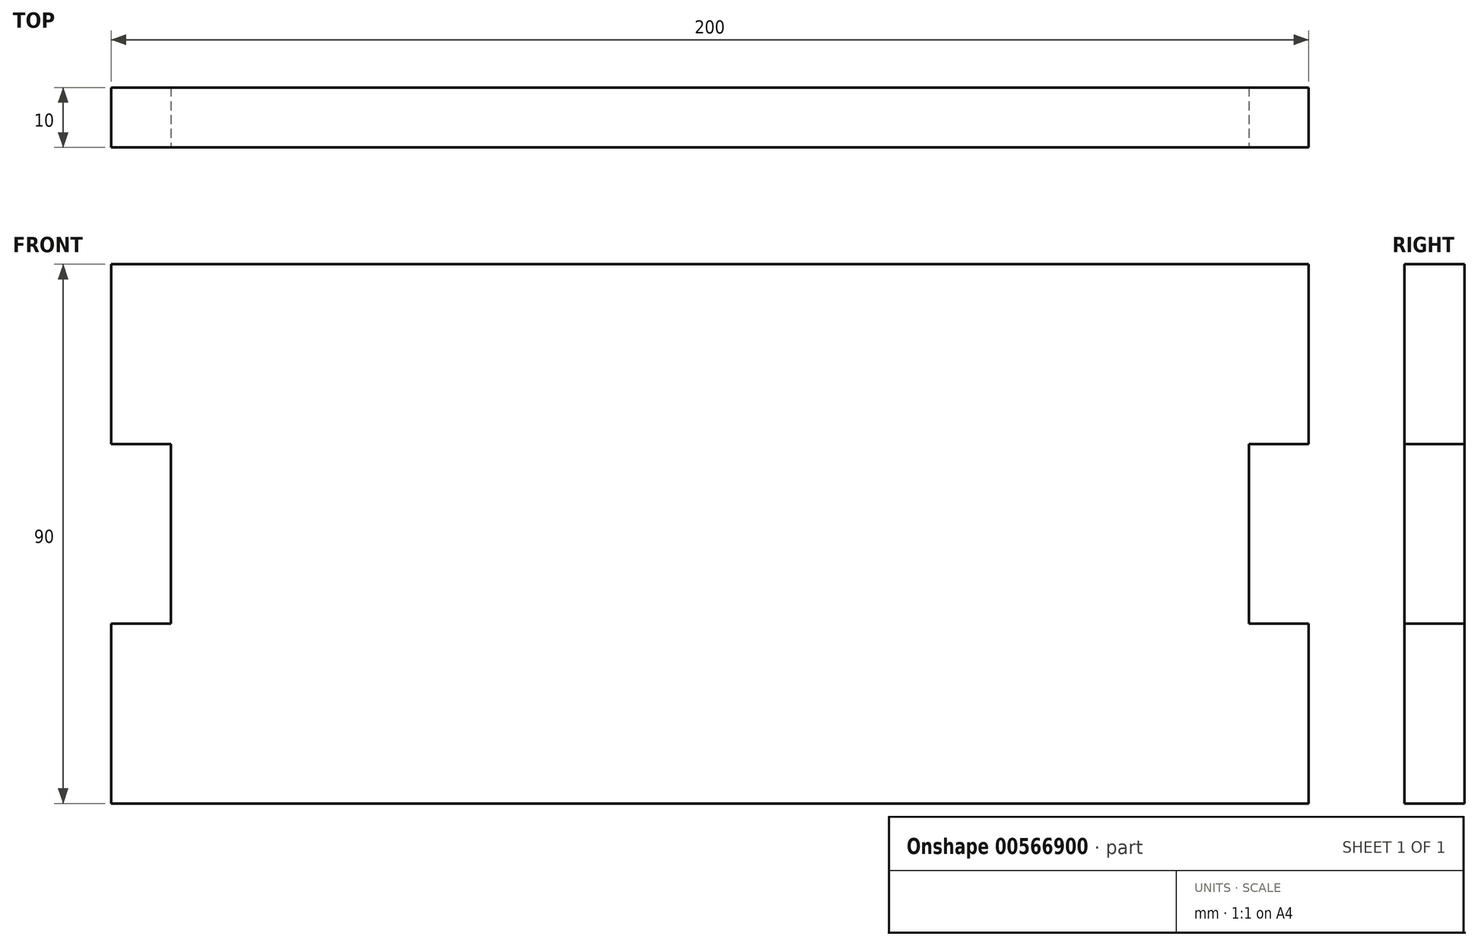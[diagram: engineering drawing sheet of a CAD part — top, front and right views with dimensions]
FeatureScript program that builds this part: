
annotation { "Feature Type Name" : "Feature", "Feature Type Description" : "" }
export const myFeature = defineFeature(function(context is Context, id is Id, definition is map)
    precondition{}
    {
        {
            var Q0;
            Q0=qCreatedBy(makeId("Front.planeOp"),FACE);
            var sketch = newSketch(context, id + "F0", { "sketchPlane" : qUnion([Q0])});
            skLineSegment(sketch, "E0", {"start": v(0, 0) * mm, "end": v(100, 0) * mm});
            skLineSegment(sketch, "E1", {"start": v(100, 0) * mm, "end": v(100, 90) * mm, "construction": true});
            skLineSegment(sketch, "E2", {"start": v(100, 90) * mm, "end": v(0, 90) * mm});
            skLineSegment(sketch, "E3", {"start": v(0, 90) * mm, "end": v(0, 60) * mm});
            skLineSegment(sketch, "E4", {"start": v(0, 0) * mm, "end": v(0, 30) * mm});
            skLineSegment(sketch, "E5", {"start": v(0, 30) * mm, "end": v(10, 30) * mm});
            skLineSegment(sketch, "E6", {"start": v(10, 30) * mm, "end": v(10, 60) * mm});
            skLineSegment(sketch, "E7", {"start": v(10, 60) * mm, "end": v(0, 60) * mm});
            skLineSegment(sketch, "E8.MirrorCS", {"start": v(200, 90) * mm, "end": v(200, 60) * mm});
            skLineSegment(sketch, "E9.MirrorCS", {"start": v(200, 0) * mm, "end": v(100, 0) * mm});
            skLineSegment(sketch, "E10.MirrorCS", {"start": v(190, 60) * mm, "end": v(200, 60) * mm});
            skLineSegment(sketch, "E11.MirrorCS", {"start": v(100, 90) * mm, "end": v(200, 90) * mm});
            skLineSegment(sketch, "E12.MirrorCS", {"start": v(200, 0) * mm, "end": v(200, 30) * mm});
            skLineSegment(sketch, "E13.MirrorCS", {"start": v(190, 30) * mm, "end": v(190, 60) * mm});
            skLineSegment(sketch, "E14.MirrorCS", {"start": v(200, 30) * mm, "end": v(190, 30) * mm});
            skSolve(sketch);
        }
        {
            var Q0;
            Q0=makeQuery(id+"F0.imprint","IMPRINT",FACE,{"disambiguationData":[TD([[makeQuery(id+"F0.imprint","IMPRINT",EDGE,{"derivedFrom":sQuery(id+"F0.wireOp",EDGE,"E0")}),1.0]])]});
            extrude(context, id + "F1", {"entities" : qUnion([Q0]), "oppositeDirection" : true, "depth" : 10 * mm, "offsetDistance" : 25 * mm});
        }
    });
